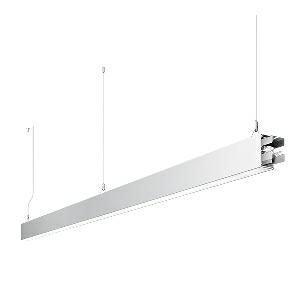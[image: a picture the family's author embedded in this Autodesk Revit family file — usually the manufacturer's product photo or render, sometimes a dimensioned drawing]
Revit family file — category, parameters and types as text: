
# Revit family: idoo_line_-_ilp_6000_840_d_sta_00805702_93f7
name_source: partatom
category: Lighting Fixtures
units: mm (PartAtom-declared; Revit-internal decimal feet)

## family parameters
Cut with Voids When Loaded = No
Host = Face
Light Source = No
Part Type = Normal
Room Calculation Point = No
Round Connector Dimension = Use Diameter
Shared = No

## types (1)
- IDOO.line - ILP 6000/840/D STA (1 x LED, 6300 lm, 4000K)
    Apparent Load = 46 VA
    Approval mark = CE
    CIE Flux Codes = 66 91 98 40 100
    Color Rendering = 80-89
    Color Temperature = 4000K
    Control Gear = Electronic ballast
    Default Elevation = 1800 mm
    Description = ILP 6000/840/D|Suspended luminaire|light source: LED|connected load: 220-240 V, 50/60 Hz|Power consumption: approx. 46 W|standby: approx. 0,15|luminous flux: 6300 lm|luminous efficacy: 136 lm/W|light distribution: Direct/indirect|direct ratio: approx. 40 %|colour temperature: Cold white, ca. 4000 K|color rendering index (CRI): >= 80|chromaticity tolerance:  3 SDCM|System of protection: IP 40|technology: Continuously dimmable|luminaire body|material: Sectional aluminium|colour: White|lamp cover: Acrylic (PMMA), Clear|mains lead: 2.00 m With free stranded wires|Fastening: Steel cable 0.3 - 0.7 m|glare control: Prism aperture|luminance(L65): <= 2700 cd/m|unified glare rating(4H 8H): <=  16|special features: DALI Load 1x, TouchDIM - dimming via standard switch, Through-wired, up to 18 m on one mains connection, Flicker-free, Suitable as emergency lighting, Start luminaire with mains connection, Mechanical and electrical connection of the individual modules without tools|
    Frequency = 50 Hz
    Height = 110 mm
    Lamp = 1 x LED
    Lamp Light Flux = 6300 lm
    Lamp count = 1
    Length = 2250 mm
    Luminous efficacy = 137 lm/W
    Manufacturer = Waldmann
    ModVariant = No
    Model = 00805702
    Mounting Place = Ceiling
    Mounting Type = Pendant
    Number of Poles = 1
    OnlyDefault = Yes
    Power Factor = 1
    Product Name = IDOO.line - ILP 6000/840/D STA
    Product group = Suspended luminaire
    ProductGroupID = 9
    Protection Class = Protection class I
    Protection Degree = IP 40
    RLX_Detail_Level = 1
    RLX_Emergency_Light_Flux = 0 lm
    RLX_Emergency_Type = 0
    RLX_Emergency_Type_DB = No
    RlxData = <blob elided: 22905 chars, md5=c3ecbae1>
    Socket = socket
    Standby Power = 0 W
    System Light Flux = 6300 lm
    System Power = 46 W
    Type Comments = Product without accessories
    Type Image = 113313000-00692603.jpg
    URL = http://relux.com
    VarID = ---
    Voltage = 230 V
    Voltage Range = 220-240 V
    Weight = 0.00 kg
    Width = 60 mm  [stored 0.19685 ft]

note: [stored X ft] marks values corroborated as IEEE doubles in the binary element streams (Revit-internal decimal feet)

## geometry (parser evidence)
native form markers: Blend x4, Sweep x13
no freeform markers — native parametric forms only
